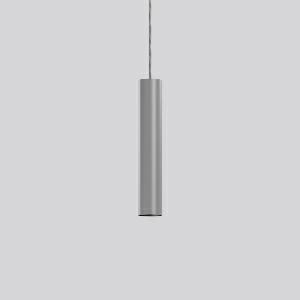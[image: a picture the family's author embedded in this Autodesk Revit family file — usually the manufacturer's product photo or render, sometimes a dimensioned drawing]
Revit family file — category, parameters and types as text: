
# Revit family: deecos_p_micro_911491_004_1_30b2
name_source: partatom
category: Lighting Fixtures
units: mm (PartAtom-declared; Revit-internal decimal feet)

## family parameters
Cut with Voids When Loaded = No
Host = Face
Light Source = No
Part Type = Normal
Room Calculation Point = No
Round Connector Dimension = Use Diameter
Shared = No

## types (1)
- DEECOS P micro (1 x LED Modul 930, 1750 lm, 3000)
    Apparent Load = 16 VA
    CIE Flux Codes = 98 100 100 100 100
    Color Rendering = 90
    Color Temperature = 3000
    Default Elevation = 1800 mm
    Description = Series: DEECOS P micro
Cylindrical pendant luminaire. Housing: die-cast aluminium, powder-coated. Canopy made of powder-coated sheet steel with magnetic attachment. Optical assembly with reflector made of MIRO-Silver with 98% total light reflection for outstanding efficiency - can be changed without tools. Black plastic ring and recessed LED to prevent glare from the side. Best colour rendering index Ra>90. Transparent suspension cable 3 m, can be shortened. High quality converter without flickering and stroboscopic effect. 
Colour: silver
Diameter: 60 mm
Height: 340 mm
Suspension length: 3000 mm
Lamp: LED
Socket: without socket
Colour temperature: 3000K
Colour rendering index (CRI): 92
System power: 16 W
Rated luminous flux: 1750 lm
Luminous efficiency: 109 lm/W
Control gear: Regulated power supply
Protection class: I
Type of protection: IP 20
    Height = 340 mm
    Lamp = 1 x LED Modul 930
    Lamp Light Flux = 1750 lm
    Lamp count = 1
    Length = 60 mm  [stored 0.19685 ft]
    Lifetime = 50000 h
    Luminous efficacy = 109 lm/W
    Manufacturer = RZB
    ModVariant = No
    Model = 911491.004.1
    Mounting Place = Ceiling
    Mounting Type = Pendant
    Number of Poles = 1
    OnlyDefault = Yes
    Power Factor = 1
    Product Name = DEECOS P micro
    Product group = Pendant luminaires
    ProductGroupID = 902
    Protection Class = Protection class I
    Protection Degree = Degree of protection
    RLX_Detail_Level = 1
    RLX_Emergency_Light_Flux = 0 lm
    RLX_Emergency_Type = 0
    RLX_Emergency_Type_DB = No
    RlxData = <blob elided: 31013 chars, md5=747a4ee0>
    Socket = socket
    Standby Power = 0 W
    System Light Flux = 1750 lm
    System Power = 16 W
    Type Comments = Product without accessories
    Type Image = 911491.004.jpg
    URL = http://relux.com
    VarID = ---
    Voltage = 0 V
    Weight = 0.00 kg
    Width = 0 mm  [stored 0 ft]

note: [stored X ft] marks values corroborated as IEEE doubles in the binary element streams (Revit-internal decimal feet)

## geometry (parser evidence)
native form markers: Blend x4, Sweep x11
no freeform markers — native parametric forms only
